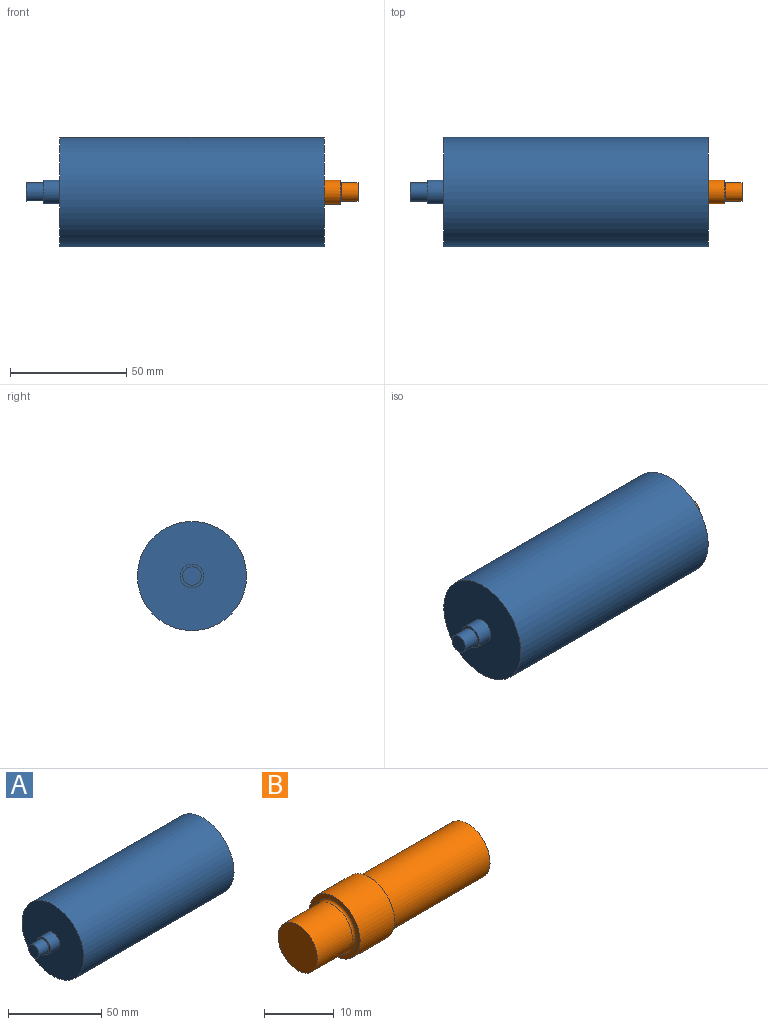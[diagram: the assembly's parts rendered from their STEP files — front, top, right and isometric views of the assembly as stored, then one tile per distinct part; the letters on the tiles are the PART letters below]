
ASSEMBLY  parts=2 mates=1
PART A: 9 faces, bbox 128.5x47x47 mm
  f0: plane 47x47mm, normal (1,0,0), area 1671.3mm2, adj f1,f7
  f1: cylinder r=23.5mm len=114mm, axis (-1,0,0), area 16832.7mm2, adj f0,f2
  f2: plane 47x47mm, normal (-1,0,0), area 1651.6mm2, adj f1,f3
  f3: cylinder r=5.15mm len=10.3mm, axis (-1,0,0), area 226.5mm2, adj f2,f4
  f4: plane 10.3x10.3mm, normal (-1,0,0), area 33.1mm2, adj f3,f5
  f5: cylinder r=4mm len=8mm, axis (-1,0,0), area 188.5mm2, adj f4,f6
  f6: plane 8x8mm, normal (-1,0,0), area 50.3mm2, adj f5
  f7: cylinder r=4.5mm len=20mm, axis (1,0,0), area 565.5mm2, adj f0,f8
  f8: plane 9x9mm, normal (1,0,0), area 63.6mm2, adj f7
PART B: 9 faces, bbox 34.5x10.6x10.6 mm
  f0: plane 8x8mm, normal (-1,0,0), area 50.3mm2, adj f6
  f1: plane 9x9mm, normal (1,0,0), area 63.6mm2, adj f2
  f2: cylinder r=4.5mm len=19.6mm, axis (-1,0,0), area 554.2mm2, adj f1,f8
  f3: plane 10.3x10.3mm, normal (1,0,0), area 7.9mm2, adj f4,f8
  f4: cylinder r=5.15mm len=10.3mm, axis (-1,0,0), area 226.5mm2, adj f3,f5
  f5: plane 10.3x10.3mm, normal (-1,0,0), area 22.5mm2, adj f4,f7
  f6: cylinder r=4mm len=8mm, axis (-1,0,0), area 178.4mm2, adj f0,f7
  f7: torus R=4.4mm, axis (-1,0,0), area 16.4mm2, adj f5,f6
  f8: torus R=4.9mm, axis (-1,0,0), area 18.3mm2, adj f2,f3
PLACE A t=(-47.88,-9.16,-4.18)mm
PLACE B rot(axis=(0,0.71,0.71),180deg) t=(80.62,-9.16,-4.18)mm
MATE fastened B.f2 <-> A.f1  axis (-1,0,0) through (66.12,-9.16,-4.18)mm
